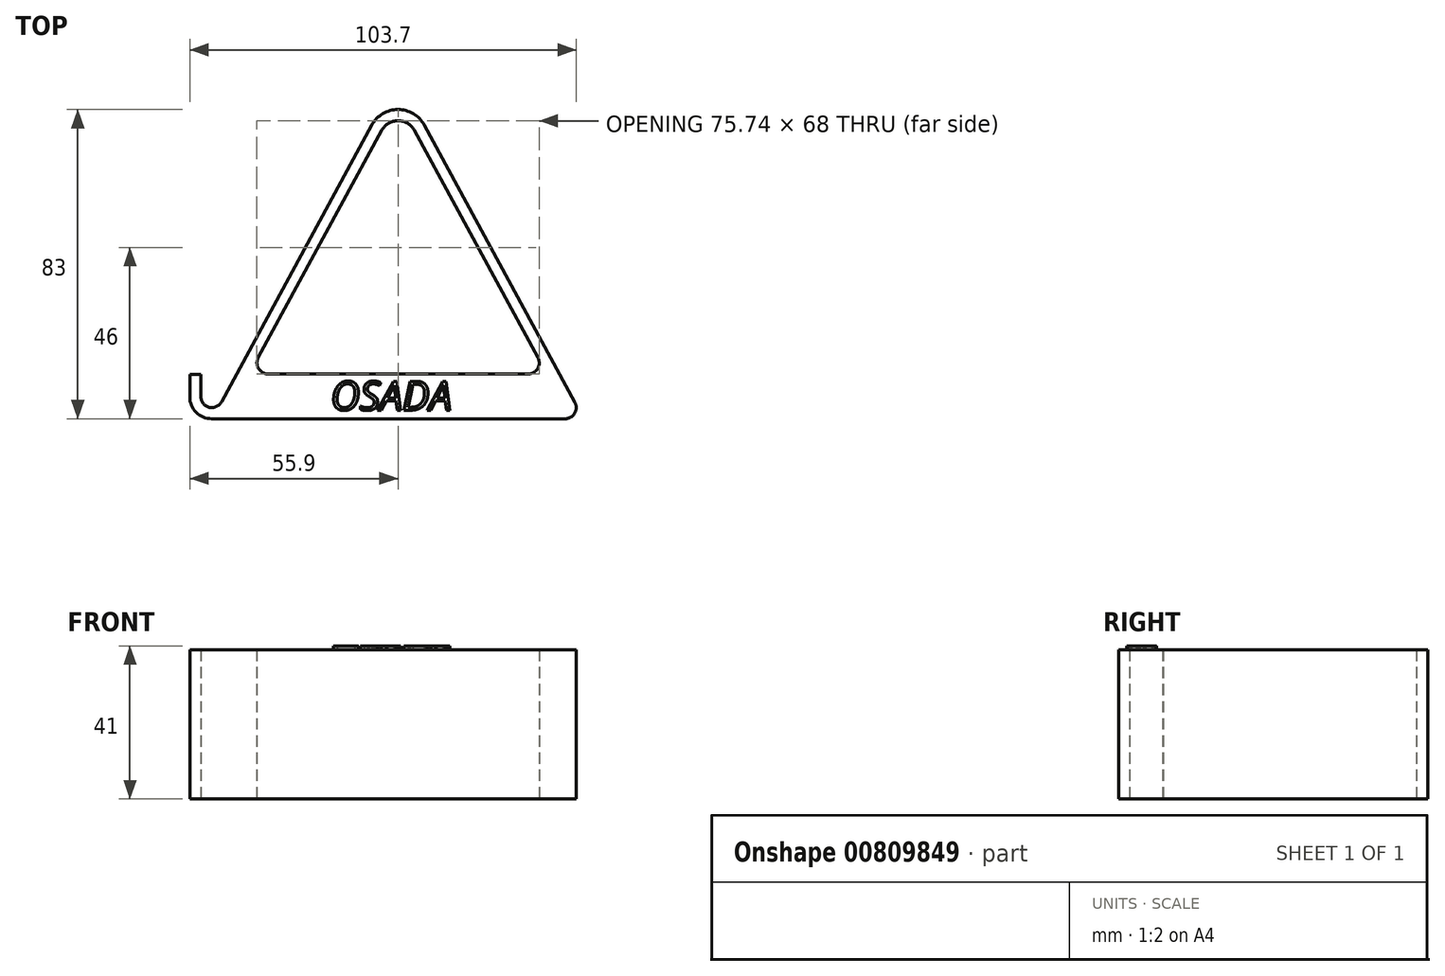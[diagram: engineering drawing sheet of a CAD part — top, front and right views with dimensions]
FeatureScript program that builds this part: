
annotation { "Feature Type Name" : "Feature", "Feature Type Description" : "" }
export const myFeature = defineFeature(function(context is Context, id is Id, definition is map)
    precondition{}
    {
        {
            var Q0;
            Q0=qCreatedBy(makeId("Top.planeOp"),FACE);
            var sketch = newSketch(context, id + "F0", { "sketchPlane" : qUnion([Q0])});
            skArc(sketch, "E0", {"start": v(54.4, 71.39) * mm, "mid": v(50, 74) * mm, "end": v(45.6, 71.39) * mm});
            skLineSegment(sketch, "E1", {"start": v(0, -6) * mm, "end": v(94.8, -6) * mm});
            skLineSegment(sketch, "E2", {"start": v(50, 74) * mm, "end": v(50, -6) * mm});
            skLineSegment(sketch, "E3", {"start": v(12.5, 10.43) * mm, "end": v(45.6, 71.39) * mm});
            skLineSegment(sketch, "E4.MirrorCS", {"start": v(96.43, -6) * mm, "end": v(96.23, -5.64) * mm});
            skPoint(sketch, "E5.orphan", {"position": v(0, -6) * mm});
            skPoint(sketch, "E6.orphan", {"position": v(3.57, -6) * mm});
            skLineSegment(sketch, "E7", {"start": v(15.13, 6) * mm, "end": v(84.87, 6) * mm});
            skLineSegment(sketch, "E8", {"start": v(-5.9, -0.1) * mm, "end": v(-5.9, 5.9) * mm});
            skPoint(sketch, "E9.orphan", {"position": v(0, 6) * mm});
            skArc(sketch, "E10.trimOffspring", {"start": v(-5.9, -0.1) * mm, "mid": v(-4.17, -4.27) * mm, "end": v(0, -6) * mm});
            skLineSegment(sketch, "E11.0", {"start": v(97.44, -1.57) * mm, "end": v(57.03, 72.82) * mm});
            skArc(sketch, "E11.1", {"start": v(57.03, 72.82) * mm, "mid": v(50, 77) * mm, "end": v(42.97, 72.82) * mm});
            skLineSegment(sketch, "E11.2", {"start": v(-2.9, -0.1) * mm, "end": v(-2.9, 5.9) * mm});
            skArc(sketch, "E11.3", {"start": v(-2.9, -0.1) * mm, "mid": v(-2.05, -2.15) * mm, "end": v(0, -3) * mm});
            skArc(sketch, "E11.4", {"start": v(2.64, -1.43) * mm, "mid": v(1.53, -2.58) * mm, "end": v(0, -3) * mm});
            skLineSegment(sketch, "E11.5", {"start": v(2.64, -1.43) * mm, "end": v(42.97, 72.82) * mm});
            skPoint(sketch, "E12.visualSharp", {"position": v(99.85, -6) * mm});
            skArc(sketch, "E12.filletArc", {"start": v(94.8, -6) * mm, "mid": v(97.38, -4.53) * mm, "end": v(97.44, -1.57) * mm});
            skLineSegment(sketch, "E13.trimOffspring", {"start": v(87.5, 10.43) * mm, "end": v(54.4, 71.39) * mm});
            skLineSegment(sketch, "E14", {"start": v(-5.9, 5.9) * mm, "end": v(-2.9, 5.9) * mm});
            skPoint(sketch, "E15.visualSharp", {"position": v(10.09, 6) * mm});
            skArc(sketch, "E15.filletArc", {"start": v(12.5, 10.43) * mm, "mid": v(12.55, 7.47) * mm, "end": v(15.13, 6) * mm});
            skPoint(sketch, "E16.visualSharp", {"position": v(89.91, 6) * mm});
            skArc(sketch, "E16.filletArc", {"start": v(84.87, 6) * mm, "mid": v(87.45, 7.47) * mm, "end": v(87.5, 10.43) * mm});
            skSolve(sketch);
        }
        {
            var Q0;
            Q0 = qSketchRegion(id + "F0", true);
            extrude(context, id + "F1", {"entities" : qUnion([Q0]), "depth" : 40 * mm, "offsetDistance" : 25 * mm});
        }
        {
            var Q0;
            Q0=makeQuery(id+"F1.opExtrude","CAP_FACE",FACE,{"disambiguationData":[OSD([sQuery(id+"F0.wireOp",EDGE,"E0"),sQuery(id+"F0.wireOp",EDGE,"E1"),sQuery(id+"F0.wireOp",EDGE,"E3"),sQuery(id+"F0.wireOp",EDGE,"E7"),sQuery(id+"F0.wireOp",EDGE,"E8"),sQuery(id+"F0.wireOp",EDGE,"E10.trimOffspring"),sQuery(id+"F0.wireOp",EDGE,"E11.0"),sQuery(id+"F0.wireOp",EDGE,"E11.1"),sQuery(id+"F0.wireOp",EDGE,"E11.2"),sQuery(id+"F0.wireOp",EDGE,"E11.3"),sQuery(id+"F0.wireOp",EDGE,"E11.4"),sQuery(id+"F0.wireOp",EDGE,"E11.5"),sQuery(id+"F0.wireOp",EDGE,"E12.filletArc"),sQuery(id+"F0.wireOp",EDGE,"E13.trimOffspring"),sQuery(id+"F0.wireOp",EDGE,"E14"),sQuery(id+"F0.wireOp",EDGE,"E15.filletArc"),sQuery(id+"F0.wireOp",EDGE,"E16.filletArc")])],"isStart":false});
            var sketch = newSketch(context, id + "F2", { "sketchPlane" : qUnion([Q0])});
            skText(sketch, "E17", { "text": "OSADA", "fontName": "OpenSans-Italic.ttf"});
            const initialGuessF2  = {"E17": [0.0319, -0.0037, 1, 0, 0.0078]};
            skSetInitialGuess(sketch, initialGuessF2);
            skSolve(sketch);
        }
        {
            var Q0;
            Q0 = qSketchRegion(id + "F2", true);
            extrude(context, id + "F3", {"entities" : qUnion([Q0]), "operationType" : NewBodyOperationType.ADD, "depth" : 1 * mm, "offsetDistance" : 25 * mm});
        }
    });
